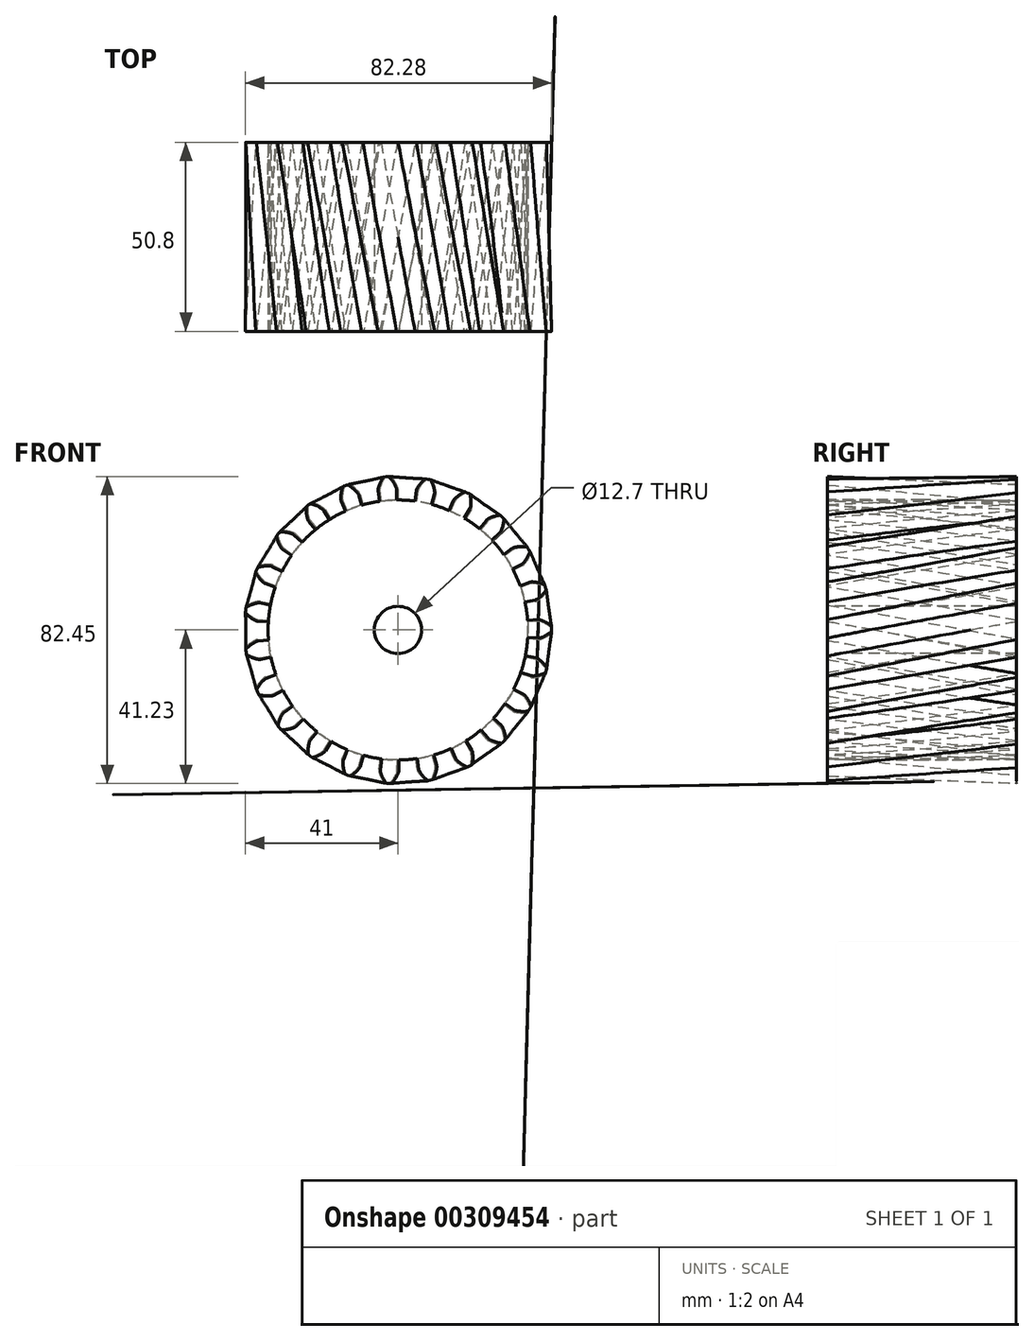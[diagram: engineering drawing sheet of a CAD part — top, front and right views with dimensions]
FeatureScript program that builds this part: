
annotation { "Feature Type Name" : "Feature", "Feature Type Description" : "" }
export const myFeature = defineFeature(function(context is Context, id is Id, definition is map)
    precondition{}
    {
        {
            var Q0;
            Q0=qCreatedBy(makeId("Front.planeOp"),FACE);
            var sketch = newSketch(context, id + "F0", { "sketchPlane" : qUnion([Q0])});
            skCircle(sketch, "E0", {"center": v(0, 0) * mm, "radius": 34.92 * mm});
            skArc(sketch, "E1", {"start": v(-0.13, 38.42) * mm, "mid": v(-0.86, 39.8) * mm, "end": v(-1.8, 41.05) * mm});
            skLineSegment(sketch, "E2", {"start": v(-2.2, 41.22) * mm, "end": v(-2.7, 41.2) * mm});
            skLineSegment(sketch, "E3", {"start": v(0, 37.79) * mm, "end": v(0, 34.92) * mm});
            skLineSegment(sketch, "E4.MirrorCS", {"start": v(-3.2, 41.15) * mm, "end": v(-2.7, 41.2) * mm});
            skArc(sketch, "E5.MirrorCS", {"start": v(-4.89, 38.1) * mm, "mid": v(-4.34, 39.57) * mm, "end": v(-3.57, 40.93) * mm});
            skLineSegment(sketch, "E6.MirrorCS", {"start": v(-4.93, 37.47) * mm, "end": v(-4.56, 34.63) * mm});
            skPoint(sketch, "E7.visualSharp", {"position": v(-4.97, 37.77) * mm});
            skArc(sketch, "E7.filletArc", {"start": v(-4.89, 38.1) * mm, "mid": v(-4.94, 37.79) * mm, "end": v(-4.93, 37.47) * mm});
            skPoint(sketch, "E8.visualSharp", {"position": v(0, 38.1) * mm});
            skArc(sketch, "E8.filletArc", {"start": v(0, 37.79) * mm, "mid": v(-0.03, 38.1) * mm, "end": v(-0.13, 38.42) * mm});
            skPoint(sketch, "E9.visualSharp", {"position": v(-3.43, 41.13) * mm});
            skArc(sketch, "E9.filletArc", {"start": v(-3.2, 41.15) * mm, "mid": v(-3.4, 41.09) * mm, "end": v(-3.57, 40.93) * mm});
            skPoint(sketch, "E10.visualSharp", {"position": v(-1.97, 41.23) * mm});
            skArc(sketch, "E10.filletArc", {"start": v(-1.8, 41.05) * mm, "mid": v(-1.99, 41.18) * mm, "end": v(-2.2, 41.22) * mm});
            skSolve(sketch);
        }
        {
            var Q0;
            Q0=qCreatedBy(makeId("Front.planeOp"),FACE);
            cPlane(context, id + "F1", {"entities" : qUnion([Q0]), "cplaneType" : CPlaneType.OFFSET, "offset" : 50.8 * mm, "width" : 152.4 * mm, "height" : 152.4 * mm});
        }
        {
            var Q0;
            Q0=qCreatedBy(id+"F1.planeOp",FACE);
            var sketch = newSketch(context, id + "F2", { "sketchPlane" : qUnion([Q0])});
            skCircle(sketch, "E11", {"center": v(0, 0) * mm, "radius": 34.92 * mm});
            skArc(sketch, "E12", {"start": v(-0.13, 38.42) * mm, "mid": v(-0.86, 39.8) * mm, "end": v(-1.8, 41.05) * mm});
            skLineSegment(sketch, "E13", {"start": v(-2.2, 41.22) * mm, "end": v(-2.7, 41.2) * mm});
            skLineSegment(sketch, "E14", {"start": v(0, 37.79) * mm, "end": v(0, 34.92) * mm});
            skLineSegment(sketch, "E15.MirrorCS", {"start": v(-3.2, 41.15) * mm, "end": v(-2.7, 41.2) * mm});
            skArc(sketch, "E16.MirrorCS", {"start": v(-4.89, 38.1) * mm, "mid": v(-4.34, 39.57) * mm, "end": v(-3.57, 40.93) * mm});
            skLineSegment(sketch, "E17.MirrorCS", {"start": v(-4.93, 37.47) * mm, "end": v(-4.56, 34.63) * mm});
            skPoint(sketch, "E18.visualSharp", {"position": v(-4.97, 37.77) * mm});
            skArc(sketch, "E18.filletArc", {"start": v(-4.89, 38.1) * mm, "mid": v(-4.94, 37.79) * mm, "end": v(-4.93, 37.47) * mm});
            skPoint(sketch, "E19.visualSharp", {"position": v(0, 38.1) * mm});
            skArc(sketch, "E19.filletArc", {"start": v(0, 37.79) * mm, "mid": v(-0.03, 38.1) * mm, "end": v(-0.13, 38.42) * mm});
            skPoint(sketch, "E20.visualSharp", {"position": v(-3.43, 41.13) * mm});
            skArc(sketch, "E20.filletArc", {"start": v(-3.2, 41.15) * mm, "mid": v(-3.4, 41.09) * mm, "end": v(-3.57, 40.93) * mm});
            skPoint(sketch, "E21.visualSharp", {"position": v(-1.97, 41.23) * mm});
            skArc(sketch, "E21.filletArc", {"start": v(-1.8, 41.05) * mm, "mid": v(-1.99, 41.18) * mm, "end": v(-2.2, 41.22) * mm});
            skLineSegment(sketch, "E22.1.0", {"start": v(-13.73, 38.92) * mm, "end": v(-13.27, 39.1) * mm});
            skLineSegment(sketch, "E22.1.1", {"start": v(-12.8, 39.24) * mm, "end": v(-13.27, 39.1) * mm});
            skArc(sketch, "E22.1.2", {"start": v(-12.37, 39.18) * mm, "mid": v(-12.58, 39.26) * mm, "end": v(-12.8, 39.24) * mm});
            skArc(sketch, "E22.1.3", {"start": v(-13.73, 38.92) * mm, "mid": v(-13.92, 38.8) * mm, "end": v(-14.04, 38.62) * mm});
            skArc(sketch, "E22.1.4", {"start": v(-14.58, 35.54) * mm, "mid": v(-14.44, 37.1) * mm, "end": v(-14.04, 38.62) * mm});
            skArc(sketch, "E22.1.5", {"start": v(-10.07, 37.07) * mm, "mid": v(-11.13, 38.22) * mm, "end": v(-12.37, 39.18) * mm});
            skArc(sketch, "E22.1.6", {"start": v(-9.78, 36.5) * mm, "mid": v(-9.9, 36.8) * mm, "end": v(-10.07, 37.07) * mm});
            skArc(sketch, "E22.1.7", {"start": v(-14.58, 35.54) * mm, "mid": v(-14.55, 35.22) * mm, "end": v(-14.46, 34.91) * mm});
            skLineSegment(sketch, "E22.1.8", {"start": v(-14.46, 34.91) * mm, "end": v(-13.37, 32.27) * mm});
            skLineSegment(sketch, "E22.1.9", {"start": v(-9.78, 36.5) * mm, "end": v(-9.04, 33.73) * mm});
            skLineSegment(sketch, "E22.2.0", {"start": v(-23.34, 34.04) * mm, "end": v(-22.93, 34.32) * mm});
            skLineSegment(sketch, "E22.2.1", {"start": v(-22.52, 34.6) * mm, "end": v(-22.93, 34.32) * mm});
            skArc(sketch, "E22.2.2", {"start": v(-22.09, 34.65) * mm, "mid": v(-22.31, 34.67) * mm, "end": v(-22.52, 34.6) * mm});
            skArc(sketch, "E22.2.3", {"start": v(-23.34, 34.04) * mm, "mid": v(-23.49, 33.88) * mm, "end": v(-23.56, 33.67) * mm});
            skArc(sketch, "E22.2.4", {"start": v(-23.28, 30.56) * mm, "mid": v(-23.55, 32.1) * mm, "end": v(-23.56, 33.67) * mm});
            skArc(sketch, "E22.2.5", {"start": v(-19.32, 33.2) * mm, "mid": v(-20.64, 34.04) * mm, "end": v(-22.09, 34.65) * mm});
            skArc(sketch, "E22.2.6", {"start": v(-18.9, 32.73) * mm, "mid": v(-19.08, 32.99) * mm, "end": v(-19.32, 33.2) * mm});
            skArc(sketch, "E22.2.7", {"start": v(-23.28, 30.56) * mm, "mid": v(-23.17, 30.25) * mm, "end": v(-23, 29.98) * mm});
            skLineSegment(sketch, "E22.2.8", {"start": v(-23, 29.98) * mm, "end": v(-21.26, 27.7) * mm});
            skLineSegment(sketch, "E22.2.9", {"start": v(-18.9, 32.73) * mm, "end": v(-17.46, 30.25) * mm});
            skLineSegment(sketch, "E22.3.0", {"start": v(-31.35, 26.84) * mm, "end": v(-31.04, 27.22) * mm});
            skLineSegment(sketch, "E22.3.1", {"start": v(-30.7, 27.58) * mm, "end": v(-31.04, 27.22) * mm});
            skArc(sketch, "E22.3.2", {"start": v(-30.3, 27.75) * mm, "mid": v(-30.52, 27.71) * mm, "end": v(-30.7, 27.58) * mm});
            skArc(sketch, "E22.3.3", {"start": v(-31.35, 26.84) * mm, "mid": v(-31.46, 26.65) * mm, "end": v(-31.47, 26.42) * mm});
            skArc(sketch, "E22.3.4", {"start": v(-30.4, 23.49) * mm, "mid": v(-31.05, 24.91) * mm, "end": v(-31.47, 26.42) * mm});
            skArc(sketch, "E22.3.5", {"start": v(-27.26, 27.07) * mm, "mid": v(-28.75, 27.54) * mm, "end": v(-30.3, 27.75) * mm});
            skArc(sketch, "E22.3.6", {"start": v(-26.72, 26.72) * mm, "mid": v(-26.97, 26.92) * mm, "end": v(-27.26, 27.07) * mm});
            skArc(sketch, "E22.3.7", {"start": v(-30.4, 23.49) * mm, "mid": v(-30.21, 23.22) * mm, "end": v(-29.98, 23) * mm});
            skLineSegment(sketch, "E22.3.8", {"start": v(-29.98, 23) * mm, "end": v(-27.7, 21.26) * mm});
            skLineSegment(sketch, "E22.3.9", {"start": v(-26.72, 26.72) * mm, "end": v(-24.7, 24.7) * mm});
            skLineSegment(sketch, "E22.4.0", {"start": v(-37.23, 17.81) * mm, "end": v(-37.02, 18.26) * mm});
            skLineSegment(sketch, "E22.4.1", {"start": v(-36.8, 18.7) * mm, "end": v(-37.02, 18.26) * mm});
            skArc(sketch, "E22.4.2", {"start": v(-36.45, 18.96) * mm, "mid": v(-36.66, 18.87) * mm, "end": v(-36.8, 18.7) * mm});
            skArc(sketch, "E22.4.3", {"start": v(-37.23, 17.81) * mm, "mid": v(-37.28, 17.6) * mm, "end": v(-37.23, 17.38) * mm});
            skArc(sketch, "E22.4.4", {"start": v(-35.44, 14.82) * mm, "mid": v(-36.44, 16.02) * mm, "end": v(-37.23, 17.38) * mm});
            skArc(sketch, "E22.4.5", {"start": v(-33.33, 19.1) * mm, "mid": v(-34.9, 19.16) * mm, "end": v(-36.45, 18.96) * mm});
            skArc(sketch, "E22.4.6", {"start": v(-32.73, 18.9) * mm, "mid": v(-33.02, 19.03) * mm, "end": v(-33.33, 19.1) * mm});
            skArc(sketch, "E22.4.7", {"start": v(-35.44, 14.82) * mm, "mid": v(-35.2, 14.61) * mm, "end": v(-34.91, 14.46) * mm});
            skLineSegment(sketch, "E22.4.8", {"start": v(-34.91, 14.46) * mm, "end": v(-32.27, 13.37) * mm});
            skLineSegment(sketch, "E22.4.9", {"start": v(-32.73, 18.9) * mm, "end": v(-30.25, 17.46) * mm});
            skLineSegment(sketch, "E22.5.0", {"start": v(-40.58, 7.57) * mm, "end": v(-40.49, 8.05) * mm});
            skLineSegment(sketch, "E22.5.1", {"start": v(-40.38, 8.53) * mm, "end": v(-40.49, 8.05) * mm});
            skArc(sketch, "E22.5.2", {"start": v(-40.12, 8.88) * mm, "mid": v(-40.29, 8.74) * mm, "end": v(-40.38, 8.53) * mm});
            skArc(sketch, "E22.5.3", {"start": v(-40.58, 7.57) * mm, "mid": v(-40.57, 7.35) * mm, "end": v(-40.46, 7.15) * mm});
            skArc(sketch, "E22.5.4", {"start": v(-38.07, 5.14) * mm, "mid": v(-39.35, 6.05) * mm, "end": v(-40.46, 7.15) * mm});
            skArc(sketch, "E22.5.5", {"start": v(-37.14, 9.82) * mm, "mid": v(-38.67, 9.47) * mm, "end": v(-40.12, 8.88) * mm});
            skArc(sketch, "E22.5.6", {"start": v(-36.5, 9.78) * mm, "mid": v(-36.82, 9.83) * mm, "end": v(-37.14, 9.82) * mm});
            skArc(sketch, "E22.5.7", {"start": v(-38.07, 5.14) * mm, "mid": v(-37.78, 5) * mm, "end": v(-37.47, 4.93) * mm});
            skLineSegment(sketch, "E22.5.8", {"start": v(-37.47, 4.93) * mm, "end": v(-34.63, 4.56) * mm});
            skLineSegment(sketch, "E22.5.9", {"start": v(-36.5, 9.78) * mm, "end": v(-33.73, 9.04) * mm});
            skLineSegment(sketch, "E22.6.0", {"start": v(-41.15, -3.2) * mm, "end": v(-41.2, -2.7) * mm});
            skLineSegment(sketch, "E22.6.1", {"start": v(-41.22, -2.2) * mm, "end": v(-41.2, -2.7) * mm});
            skArc(sketch, "E22.6.2", {"start": v(-41.05, -1.8) * mm, "mid": v(-41.18, -1.99) * mm, "end": v(-41.22, -2.2) * mm});
            skArc(sketch, "E22.6.3", {"start": v(-41.15, -3.2) * mm, "mid": v(-41.09, -3.4) * mm, "end": v(-40.93, -3.57) * mm});
            skArc(sketch, "E22.6.4", {"start": v(-38.1, -4.89) * mm, "mid": v(-39.57, -4.34) * mm, "end": v(-40.93, -3.57) * mm});
            skArc(sketch, "E22.6.5", {"start": v(-38.42, -0.13) * mm, "mid": v(-39.8, -0.86) * mm, "end": v(-41.05, -1.8) * mm});
            skArc(sketch, "E22.6.6", {"start": v(-37.79, 0) * mm, "mid": v(-38.1, -0.03) * mm, "end": v(-38.42, -0.13) * mm});
            skArc(sketch, "E22.6.7", {"start": v(-38.1, -4.89) * mm, "mid": v(-37.79, -4.94) * mm, "end": v(-37.47, -4.93) * mm});
            skLineSegment(sketch, "E22.6.8", {"start": v(-37.47, -4.93) * mm, "end": v(-34.63, -4.56) * mm});
            skLineSegment(sketch, "E22.6.9", {"start": v(-37.79, 0) * mm, "end": v(-34.92, 0) * mm});
            skLineSegment(sketch, "E22.7.0", {"start": v(-38.92, -13.73) * mm, "end": v(-39.1, -13.27) * mm});
            skLineSegment(sketch, "E22.7.1", {"start": v(-39.24, -12.8) * mm, "end": v(-39.1, -13.27) * mm});
            skArc(sketch, "E22.7.2", {"start": v(-39.18, -12.37) * mm, "mid": v(-39.26, -12.58) * mm, "end": v(-39.24, -12.8) * mm});
            skArc(sketch, "E22.7.3", {"start": v(-38.92, -13.73) * mm, "mid": v(-38.8, -13.92) * mm, "end": v(-38.62, -14.04) * mm});
            skArc(sketch, "E22.7.4", {"start": v(-35.54, -14.58) * mm, "mid": v(-37.1, -14.44) * mm, "end": v(-38.62, -14.04) * mm});
            skArc(sketch, "E22.7.5", {"start": v(-37.07, -10.07) * mm, "mid": v(-38.22, -11.13) * mm, "end": v(-39.18, -12.37) * mm});
            skArc(sketch, "E22.7.6", {"start": v(-36.5, -9.78) * mm, "mid": v(-36.8, -9.9) * mm, "end": v(-37.07, -10.07) * mm});
            skArc(sketch, "E22.7.7", {"start": v(-35.54, -14.58) * mm, "mid": v(-35.22, -14.55) * mm, "end": v(-34.91, -14.46) * mm});
            skLineSegment(sketch, "E22.7.8", {"start": v(-34.91, -14.46) * mm, "end": v(-32.27, -13.37) * mm});
            skLineSegment(sketch, "E22.7.9", {"start": v(-36.5, -9.78) * mm, "end": v(-33.73, -9.04) * mm});
            skLineSegment(sketch, "E22.8.0", {"start": v(-34.04, -23.34) * mm, "end": v(-34.32, -22.93) * mm});
            skLineSegment(sketch, "E22.8.1", {"start": v(-34.6, -22.52) * mm, "end": v(-34.32, -22.93) * mm});
            skArc(sketch, "E22.8.2", {"start": v(-34.65, -22.09) * mm, "mid": v(-34.67, -22.31) * mm, "end": v(-34.6, -22.52) * mm});
            skArc(sketch, "E22.8.3", {"start": v(-34.04, -23.34) * mm, "mid": v(-33.88, -23.49) * mm, "end": v(-33.67, -23.56) * mm});
            skArc(sketch, "E22.8.4", {"start": v(-30.56, -23.28) * mm, "mid": v(-32.1, -23.55) * mm, "end": v(-33.67, -23.56) * mm});
            skArc(sketch, "E22.8.5", {"start": v(-33.2, -19.32) * mm, "mid": v(-34.04, -20.64) * mm, "end": v(-34.65, -22.09) * mm});
            skArc(sketch, "E22.8.6", {"start": v(-32.73, -18.9) * mm, "mid": v(-32.99, -19.08) * mm, "end": v(-33.2, -19.32) * mm});
            skArc(sketch, "E22.8.7", {"start": v(-30.56, -23.28) * mm, "mid": v(-30.25, -23.17) * mm, "end": v(-29.98, -23) * mm});
            skLineSegment(sketch, "E22.8.8", {"start": v(-29.98, -23) * mm, "end": v(-27.7, -21.26) * mm});
            skLineSegment(sketch, "E22.8.9", {"start": v(-32.73, -18.9) * mm, "end": v(-30.25, -17.46) * mm});
            skLineSegment(sketch, "E22.9.0", {"start": v(-26.84, -31.35) * mm, "end": v(-27.22, -31.04) * mm});
            skLineSegment(sketch, "E22.9.1", {"start": v(-27.58, -30.7) * mm, "end": v(-27.22, -31.04) * mm});
            skArc(sketch, "E22.9.2", {"start": v(-27.75, -30.3) * mm, "mid": v(-27.71, -30.52) * mm, "end": v(-27.58, -30.7) * mm});
            skArc(sketch, "E22.9.3", {"start": v(-26.84, -31.35) * mm, "mid": v(-26.65, -31.46) * mm, "end": v(-26.42, -31.47) * mm});
            skArc(sketch, "E22.9.4", {"start": v(-23.49, -30.4) * mm, "mid": v(-24.91, -31.05) * mm, "end": v(-26.42, -31.47) * mm});
            skArc(sketch, "E22.9.5", {"start": v(-27.07, -27.26) * mm, "mid": v(-27.54, -28.75) * mm, "end": v(-27.75, -30.3) * mm});
            skArc(sketch, "E22.9.6", {"start": v(-26.72, -26.72) * mm, "mid": v(-26.92, -26.97) * mm, "end": v(-27.07, -27.26) * mm});
            skArc(sketch, "E22.9.7", {"start": v(-23.49, -30.4) * mm, "mid": v(-23.22, -30.21) * mm, "end": v(-23, -29.98) * mm});
            skLineSegment(sketch, "E22.9.8", {"start": v(-23, -29.98) * mm, "end": v(-21.26, -27.7) * mm});
            skLineSegment(sketch, "E22.9.9", {"start": v(-26.72, -26.72) * mm, "end": v(-24.7, -24.7) * mm});
            skLineSegment(sketch, "E22.10.0", {"start": v(-17.81, -37.23) * mm, "end": v(-18.26, -37.02) * mm});
            skLineSegment(sketch, "E22.10.1", {"start": v(-18.7, -36.8) * mm, "end": v(-18.26, -37.02) * mm});
            skArc(sketch, "E22.10.2", {"start": v(-18.96, -36.45) * mm, "mid": v(-18.87, -36.66) * mm, "end": v(-18.7, -36.8) * mm});
            skArc(sketch, "E22.10.3", {"start": v(-17.81, -37.23) * mm, "mid": v(-17.6, -37.28) * mm, "end": v(-17.38, -37.23) * mm});
            skArc(sketch, "E22.10.4", {"start": v(-14.82, -35.44) * mm, "mid": v(-16.02, -36.44) * mm, "end": v(-17.38, -37.23) * mm});
            skArc(sketch, "E22.10.5", {"start": v(-19.1, -33.33) * mm, "mid": v(-19.16, -34.9) * mm, "end": v(-18.96, -36.45) * mm});
            skArc(sketch, "E22.10.6", {"start": v(-18.9, -32.73) * mm, "mid": v(-19.03, -33.02) * mm, "end": v(-19.1, -33.33) * mm});
            skArc(sketch, "E22.10.7", {"start": v(-14.82, -35.44) * mm, "mid": v(-14.61, -35.2) * mm, "end": v(-14.46, -34.91) * mm});
            skLineSegment(sketch, "E22.10.8", {"start": v(-14.46, -34.91) * mm, "end": v(-13.37, -32.27) * mm});
            skLineSegment(sketch, "E22.10.9", {"start": v(-18.9, -32.73) * mm, "end": v(-17.46, -30.25) * mm});
            skLineSegment(sketch, "E22.11.0", {"start": v(-7.57, -40.58) * mm, "end": v(-8.05, -40.49) * mm});
            skLineSegment(sketch, "E22.11.1", {"start": v(-8.53, -40.38) * mm, "end": v(-8.05, -40.49) * mm});
            skArc(sketch, "E22.11.2", {"start": v(-8.88, -40.12) * mm, "mid": v(-8.74, -40.29) * mm, "end": v(-8.53, -40.38) * mm});
            skArc(sketch, "E22.11.3", {"start": v(-7.57, -40.58) * mm, "mid": v(-7.35, -40.57) * mm, "end": v(-7.15, -40.46) * mm});
            skArc(sketch, "E22.11.4", {"start": v(-5.14, -38.07) * mm, "mid": v(-6.05, -39.35) * mm, "end": v(-7.15, -40.46) * mm});
            skArc(sketch, "E22.11.5", {"start": v(-9.82, -37.14) * mm, "mid": v(-9.47, -38.67) * mm, "end": v(-8.88, -40.12) * mm});
            skArc(sketch, "E22.11.6", {"start": v(-9.78, -36.5) * mm, "mid": v(-9.83, -36.82) * mm, "end": v(-9.82, -37.14) * mm});
            skArc(sketch, "E22.11.7", {"start": v(-5.14, -38.07) * mm, "mid": v(-5, -37.78) * mm, "end": v(-4.93, -37.47) * mm});
            skLineSegment(sketch, "E22.11.8", {"start": v(-4.93, -37.47) * mm, "end": v(-4.56, -34.63) * mm});
            skLineSegment(sketch, "E22.11.9", {"start": v(-9.78, -36.5) * mm, "end": v(-9.04, -33.73) * mm});
            skLineSegment(sketch, "E22.12.0", {"start": v(3.2, -41.15) * mm, "end": v(2.7, -41.2) * mm});
            skLineSegment(sketch, "E22.12.1", {"start": v(2.2, -41.22) * mm, "end": v(2.7, -41.2) * mm});
            skArc(sketch, "E22.12.2", {"start": v(1.8, -41.05) * mm, "mid": v(1.99, -41.18) * mm, "end": v(2.2, -41.22) * mm});
            skArc(sketch, "E22.12.3", {"start": v(3.2, -41.15) * mm, "mid": v(3.4, -41.09) * mm, "end": v(3.57, -40.93) * mm});
            skArc(sketch, "E22.12.4", {"start": v(4.89, -38.1) * mm, "mid": v(4.34, -39.57) * mm, "end": v(3.57, -40.93) * mm});
            skArc(sketch, "E22.12.5", {"start": v(0.13, -38.42) * mm, "mid": v(0.86, -39.8) * mm, "end": v(1.8, -41.05) * mm});
            skArc(sketch, "E22.12.6", {"start": v(0, -37.79) * mm, "mid": v(0.03, -38.1) * mm, "end": v(0.13, -38.42) * mm});
            skArc(sketch, "E22.12.7", {"start": v(4.89, -38.1) * mm, "mid": v(4.94, -37.79) * mm, "end": v(4.93, -37.47) * mm});
            skLineSegment(sketch, "E22.12.8", {"start": v(4.93, -37.47) * mm, "end": v(4.56, -34.63) * mm});
            skLineSegment(sketch, "E22.12.9", {"start": v(0, -37.79) * mm, "end": v(0, -34.92) * mm});
            skLineSegment(sketch, "E22.13.0", {"start": v(13.73, -38.92) * mm, "end": v(13.27, -39.1) * mm});
            skLineSegment(sketch, "E22.13.1", {"start": v(12.8, -39.24) * mm, "end": v(13.27, -39.1) * mm});
            skArc(sketch, "E22.13.2", {"start": v(12.37, -39.18) * mm, "mid": v(12.58, -39.26) * mm, "end": v(12.8, -39.24) * mm});
            skArc(sketch, "E22.13.3", {"start": v(13.73, -38.92) * mm, "mid": v(13.92, -38.8) * mm, "end": v(14.04, -38.62) * mm});
            skArc(sketch, "E22.13.4", {"start": v(14.58, -35.54) * mm, "mid": v(14.44, -37.1) * mm, "end": v(14.04, -38.62) * mm});
            skArc(sketch, "E22.13.5", {"start": v(10.07, -37.07) * mm, "mid": v(11.13, -38.22) * mm, "end": v(12.37, -39.18) * mm});
            skArc(sketch, "E22.13.6", {"start": v(9.78, -36.5) * mm, "mid": v(9.9, -36.8) * mm, "end": v(10.07, -37.07) * mm});
            skArc(sketch, "E22.13.7", {"start": v(14.58, -35.54) * mm, "mid": v(14.55, -35.22) * mm, "end": v(14.46, -34.91) * mm});
            skLineSegment(sketch, "E22.13.8", {"start": v(14.46, -34.91) * mm, "end": v(13.37, -32.27) * mm});
            skLineSegment(sketch, "E22.13.9", {"start": v(9.78, -36.5) * mm, "end": v(9.04, -33.73) * mm});
            skLineSegment(sketch, "E22.14.0", {"start": v(23.34, -34.04) * mm, "end": v(22.93, -34.32) * mm});
            skLineSegment(sketch, "E22.14.1", {"start": v(22.52, -34.6) * mm, "end": v(22.93, -34.32) * mm});
            skArc(sketch, "E22.14.2", {"start": v(22.09, -34.65) * mm, "mid": v(22.31, -34.67) * mm, "end": v(22.52, -34.6) * mm});
            skArc(sketch, "E22.14.3", {"start": v(23.34, -34.04) * mm, "mid": v(23.49, -33.88) * mm, "end": v(23.56, -33.67) * mm});
            skArc(sketch, "E22.14.4", {"start": v(23.28, -30.56) * mm, "mid": v(23.55, -32.1) * mm, "end": v(23.56, -33.67) * mm});
            skArc(sketch, "E22.14.5", {"start": v(19.32, -33.2) * mm, "mid": v(20.64, -34.04) * mm, "end": v(22.09, -34.65) * mm});
            skArc(sketch, "E22.14.6", {"start": v(18.9, -32.73) * mm, "mid": v(19.08, -32.99) * mm, "end": v(19.32, -33.2) * mm});
            skArc(sketch, "E22.14.7", {"start": v(23.28, -30.56) * mm, "mid": v(23.17, -30.25) * mm, "end": v(23, -29.98) * mm});
            skLineSegment(sketch, "E22.14.8", {"start": v(23, -29.98) * mm, "end": v(21.26, -27.7) * mm});
            skLineSegment(sketch, "E22.14.9", {"start": v(18.9, -32.73) * mm, "end": v(17.46, -30.25) * mm});
            skLineSegment(sketch, "E22.15.0", {"start": v(31.35, -26.84) * mm, "end": v(31.04, -27.22) * mm});
            skLineSegment(sketch, "E22.15.1", {"start": v(30.7, -27.58) * mm, "end": v(31.04, -27.22) * mm});
            skArc(sketch, "E22.15.2", {"start": v(30.3, -27.75) * mm, "mid": v(30.52, -27.71) * mm, "end": v(30.7, -27.58) * mm});
            skArc(sketch, "E22.15.3", {"start": v(31.35, -26.84) * mm, "mid": v(31.46, -26.65) * mm, "end": v(31.47, -26.42) * mm});
            skArc(sketch, "E22.15.4", {"start": v(30.4, -23.49) * mm, "mid": v(31.05, -24.91) * mm, "end": v(31.47, -26.42) * mm});
            skArc(sketch, "E22.15.5", {"start": v(27.26, -27.07) * mm, "mid": v(28.75, -27.54) * mm, "end": v(30.3, -27.75) * mm});
            skArc(sketch, "E22.15.6", {"start": v(26.72, -26.72) * mm, "mid": v(26.97, -26.92) * mm, "end": v(27.26, -27.07) * mm});
            skArc(sketch, "E22.15.7", {"start": v(30.4, -23.49) * mm, "mid": v(30.21, -23.22) * mm, "end": v(29.98, -23) * mm});
            skLineSegment(sketch, "E22.15.8", {"start": v(29.98, -23) * mm, "end": v(27.7, -21.26) * mm});
            skLineSegment(sketch, "E22.15.9", {"start": v(26.72, -26.72) * mm, "end": v(24.7, -24.7) * mm});
            skLineSegment(sketch, "E22.16.0", {"start": v(37.23, -17.81) * mm, "end": v(37.02, -18.26) * mm});
            skLineSegment(sketch, "E22.16.1", {"start": v(36.8, -18.7) * mm, "end": v(37.02, -18.26) * mm});
            skArc(sketch, "E22.16.2", {"start": v(36.45, -18.96) * mm, "mid": v(36.66, -18.87) * mm, "end": v(36.8, -18.7) * mm});
            skArc(sketch, "E22.16.3", {"start": v(37.23, -17.81) * mm, "mid": v(37.28, -17.6) * mm, "end": v(37.23, -17.38) * mm});
            skArc(sketch, "E22.16.4", {"start": v(35.44, -14.82) * mm, "mid": v(36.44, -16.02) * mm, "end": v(37.23, -17.38) * mm});
            skArc(sketch, "E22.16.5", {"start": v(33.33, -19.1) * mm, "mid": v(34.9, -19.16) * mm, "end": v(36.45, -18.96) * mm});
            skArc(sketch, "E22.16.6", {"start": v(32.73, -18.9) * mm, "mid": v(33.02, -19.03) * mm, "end": v(33.33, -19.1) * mm});
            skArc(sketch, "E22.16.7", {"start": v(35.44, -14.82) * mm, "mid": v(35.2, -14.61) * mm, "end": v(34.91, -14.46) * mm});
            skLineSegment(sketch, "E22.16.8", {"start": v(34.91, -14.46) * mm, "end": v(32.27, -13.37) * mm});
            skLineSegment(sketch, "E22.16.9", {"start": v(32.73, -18.9) * mm, "end": v(30.25, -17.46) * mm});
            skLineSegment(sketch, "E22.17.0", {"start": v(40.58, -7.57) * mm, "end": v(40.49, -8.05) * mm});
            skLineSegment(sketch, "E22.17.1", {"start": v(40.38, -8.53) * mm, "end": v(40.49, -8.05) * mm});
            skArc(sketch, "E22.17.2", {"start": v(40.12, -8.88) * mm, "mid": v(40.29, -8.74) * mm, "end": v(40.38, -8.53) * mm});
            skArc(sketch, "E22.17.3", {"start": v(40.58, -7.57) * mm, "mid": v(40.57, -7.35) * mm, "end": v(40.46, -7.15) * mm});
            skArc(sketch, "E22.17.4", {"start": v(38.07, -5.14) * mm, "mid": v(39.35, -6.05) * mm, "end": v(40.46, -7.15) * mm});
            skArc(sketch, "E22.17.5", {"start": v(37.14, -9.82) * mm, "mid": v(38.67, -9.47) * mm, "end": v(40.12, -8.88) * mm});
            skArc(sketch, "E22.17.6", {"start": v(36.5, -9.78) * mm, "mid": v(36.82, -9.83) * mm, "end": v(37.14, -9.82) * mm});
            skArc(sketch, "E22.17.7", {"start": v(38.07, -5.14) * mm, "mid": v(37.78, -5) * mm, "end": v(37.47, -4.93) * mm});
            skLineSegment(sketch, "E22.17.8", {"start": v(37.47, -4.93) * mm, "end": v(34.63, -4.56) * mm});
            skLineSegment(sketch, "E22.17.9", {"start": v(36.5, -9.78) * mm, "end": v(33.73, -9.04) * mm});
            skLineSegment(sketch, "E22.18.0", {"start": v(41.15, 3.2) * mm, "end": v(41.2, 2.7) * mm});
            skLineSegment(sketch, "E22.18.1", {"start": v(41.22, 2.2) * mm, "end": v(41.2, 2.7) * mm});
            skArc(sketch, "E22.18.2", {"start": v(41.05, 1.8) * mm, "mid": v(41.18, 1.99) * mm, "end": v(41.22, 2.2) * mm});
            skArc(sketch, "E22.18.3", {"start": v(41.15, 3.2) * mm, "mid": v(41.09, 3.4) * mm, "end": v(40.93, 3.57) * mm});
            skArc(sketch, "E22.18.4", {"start": v(38.1, 4.89) * mm, "mid": v(39.57, 4.34) * mm, "end": v(40.93, 3.57) * mm});
            skArc(sketch, "E22.18.5", {"start": v(38.42, 0.13) * mm, "mid": v(39.8, 0.86) * mm, "end": v(41.05, 1.8) * mm});
            skArc(sketch, "E22.18.6", {"start": v(37.79, 0) * mm, "mid": v(38.1, 0.03) * mm, "end": v(38.42, 0.13) * mm});
            skArc(sketch, "E22.18.7", {"start": v(38.1, 4.89) * mm, "mid": v(37.79, 4.94) * mm, "end": v(37.47, 4.93) * mm});
            skLineSegment(sketch, "E22.18.8", {"start": v(37.47, 4.93) * mm, "end": v(34.63, 4.56) * mm});
            skLineSegment(sketch, "E22.18.9", {"start": v(37.79, 0) * mm, "end": v(34.92, 0) * mm});
            skLineSegment(sketch, "E22.19.0", {"start": v(38.92, 13.73) * mm, "end": v(39.1, 13.27) * mm});
            skLineSegment(sketch, "E22.19.1", {"start": v(39.24, 12.8) * mm, "end": v(39.1, 13.27) * mm});
            skArc(sketch, "E22.19.2", {"start": v(39.18, 12.37) * mm, "mid": v(39.26, 12.58) * mm, "end": v(39.24, 12.8) * mm});
            skArc(sketch, "E22.19.3", {"start": v(38.92, 13.73) * mm, "mid": v(38.8, 13.92) * mm, "end": v(38.62, 14.04) * mm});
            skArc(sketch, "E22.19.4", {"start": v(35.54, 14.58) * mm, "mid": v(37.1, 14.44) * mm, "end": v(38.62, 14.04) * mm});
            skArc(sketch, "E22.19.5", {"start": v(37.07, 10.07) * mm, "mid": v(38.22, 11.13) * mm, "end": v(39.18, 12.37) * mm});
            skArc(sketch, "E22.19.6", {"start": v(36.5, 9.78) * mm, "mid": v(36.8, 9.9) * mm, "end": v(37.07, 10.07) * mm});
            skArc(sketch, "E22.19.7", {"start": v(35.54, 14.58) * mm, "mid": v(35.22, 14.55) * mm, "end": v(34.91, 14.46) * mm});
            skLineSegment(sketch, "E22.19.8", {"start": v(34.91, 14.46) * mm, "end": v(32.27, 13.37) * mm});
            skLineSegment(sketch, "E22.19.9", {"start": v(36.5, 9.78) * mm, "end": v(33.73, 9.04) * mm});
            skLineSegment(sketch, "E22.20.0", {"start": v(34.04, 23.34) * mm, "end": v(34.32, 22.93) * mm});
            skLineSegment(sketch, "E22.20.1", {"start": v(34.6, 22.52) * mm, "end": v(34.32, 22.93) * mm});
            skArc(sketch, "E22.20.2", {"start": v(34.65, 22.09) * mm, "mid": v(34.67, 22.31) * mm, "end": v(34.6, 22.52) * mm});
            skArc(sketch, "E22.20.3", {"start": v(34.04, 23.34) * mm, "mid": v(33.88, 23.49) * mm, "end": v(33.67, 23.56) * mm});
            skArc(sketch, "E22.20.4", {"start": v(30.56, 23.28) * mm, "mid": v(32.1, 23.55) * mm, "end": v(33.67, 23.56) * mm});
            skArc(sketch, "E22.20.5", {"start": v(33.2, 19.32) * mm, "mid": v(34.04, 20.64) * mm, "end": v(34.65, 22.09) * mm});
            skArc(sketch, "E22.20.6", {"start": v(32.73, 18.9) * mm, "mid": v(32.99, 19.08) * mm, "end": v(33.2, 19.32) * mm});
            skArc(sketch, "E22.20.7", {"start": v(30.56, 23.28) * mm, "mid": v(30.25, 23.17) * mm, "end": v(29.98, 23) * mm});
            skLineSegment(sketch, "E22.20.8", {"start": v(29.98, 23) * mm, "end": v(27.7, 21.26) * mm});
            skLineSegment(sketch, "E22.20.9", {"start": v(32.73, 18.9) * mm, "end": v(30.25, 17.46) * mm});
            skLineSegment(sketch, "E22.21.0", {"start": v(26.84, 31.35) * mm, "end": v(27.22, 31.04) * mm});
            skLineSegment(sketch, "E22.21.1", {"start": v(27.58, 30.7) * mm, "end": v(27.22, 31.04) * mm});
            skArc(sketch, "E22.21.2", {"start": v(27.75, 30.3) * mm, "mid": v(27.71, 30.52) * mm, "end": v(27.58, 30.7) * mm});
            skArc(sketch, "E22.21.3", {"start": v(26.84, 31.35) * mm, "mid": v(26.65, 31.46) * mm, "end": v(26.42, 31.47) * mm});
            skArc(sketch, "E22.21.4", {"start": v(23.49, 30.4) * mm, "mid": v(24.91, 31.05) * mm, "end": v(26.42, 31.47) * mm});
            skArc(sketch, "E22.21.5", {"start": v(27.07, 27.26) * mm, "mid": v(27.54, 28.75) * mm, "end": v(27.75, 30.3) * mm});
            skArc(sketch, "E22.21.6", {"start": v(26.72, 26.72) * mm, "mid": v(26.92, 26.97) * mm, "end": v(27.07, 27.26) * mm});
            skArc(sketch, "E22.21.7", {"start": v(23.49, 30.4) * mm, "mid": v(23.22, 30.21) * mm, "end": v(23, 29.98) * mm});
            skLineSegment(sketch, "E22.21.8", {"start": v(23, 29.98) * mm, "end": v(21.26, 27.7) * mm});
            skLineSegment(sketch, "E22.21.9", {"start": v(26.72, 26.72) * mm, "end": v(24.7, 24.7) * mm});
            skLineSegment(sketch, "E22.22.0", {"start": v(17.81, 37.23) * mm, "end": v(18.26, 37.02) * mm});
            skLineSegment(sketch, "E22.22.1", {"start": v(18.7, 36.8) * mm, "end": v(18.26, 37.02) * mm});
            skArc(sketch, "E22.22.2", {"start": v(18.96, 36.45) * mm, "mid": v(18.87, 36.66) * mm, "end": v(18.7, 36.8) * mm});
            skArc(sketch, "E22.22.3", {"start": v(17.81, 37.23) * mm, "mid": v(17.6, 37.28) * mm, "end": v(17.38, 37.23) * mm});
            skArc(sketch, "E22.22.4", {"start": v(14.82, 35.44) * mm, "mid": v(16.02, 36.44) * mm, "end": v(17.38, 37.23) * mm});
            skArc(sketch, "E22.22.5", {"start": v(19.1, 33.33) * mm, "mid": v(19.16, 34.9) * mm, "end": v(18.96, 36.45) * mm});
            skArc(sketch, "E22.22.6", {"start": v(18.9, 32.73) * mm, "mid": v(19.03, 33.02) * mm, "end": v(19.1, 33.33) * mm});
            skArc(sketch, "E22.22.7", {"start": v(14.82, 35.44) * mm, "mid": v(14.61, 35.2) * mm, "end": v(14.46, 34.91) * mm});
            skLineSegment(sketch, "E22.22.8", {"start": v(14.46, 34.91) * mm, "end": v(13.37, 32.27) * mm});
            skLineSegment(sketch, "E22.22.9", {"start": v(18.9, 32.73) * mm, "end": v(17.46, 30.25) * mm});
            skLineSegment(sketch, "E22.23.0", {"start": v(7.57, 40.58) * mm, "end": v(8.05, 40.49) * mm});
            skLineSegment(sketch, "E22.23.1", {"start": v(8.53, 40.38) * mm, "end": v(8.05, 40.49) * mm});
            skArc(sketch, "E22.23.2", {"start": v(8.88, 40.12) * mm, "mid": v(8.74, 40.29) * mm, "end": v(8.53, 40.38) * mm});
            skArc(sketch, "E22.23.3", {"start": v(7.57, 40.58) * mm, "mid": v(7.35, 40.57) * mm, "end": v(7.15, 40.46) * mm});
            skArc(sketch, "E22.23.4", {"start": v(5.14, 38.07) * mm, "mid": v(6.05, 39.35) * mm, "end": v(7.15, 40.46) * mm});
            skArc(sketch, "E22.23.5", {"start": v(9.82, 37.14) * mm, "mid": v(9.47, 38.67) * mm, "end": v(8.88, 40.12) * mm});
            skArc(sketch, "E22.23.6", {"start": v(9.78, 36.5) * mm, "mid": v(9.83, 36.82) * mm, "end": v(9.82, 37.14) * mm});
            skArc(sketch, "E22.23.7", {"start": v(5.14, 38.07) * mm, "mid": v(5, 37.78) * mm, "end": v(4.93, 37.47) * mm});
            skLineSegment(sketch, "E22.23.8", {"start": v(4.93, 37.47) * mm, "end": v(4.56, 34.63) * mm});
            skLineSegment(sketch, "E22.23.9", {"start": v(9.78, 36.5) * mm, "end": v(9.04, 33.73) * mm});
            skSolve(sketch);
        }
        {
            var Q0;
            Q0=makeQuery(id+"F0.imprint","IMPRINT",FACE,{"disambiguationData":[TD([[makeQuery(id+"F0.imprint","IMPRINT",EDGE,{"derivedFrom":sQuery(id+"F0.wireOp",EDGE,"E1")}),1.0]])]});
            var Q1;
            Q1=makeQuery(id+"F2.imprint","IMPRINT",FACE,{"disambiguationData":[TD([[makeQuery(id+"F2.imprint","IMPRINT",EDGE,{"derivedFrom":sQuery(id+"F2.wireOp",EDGE,"E22.23.0")}),-1.0]])]});
            loft(context, id + "F3", {"sheetProfilesArray" : [{ "sheetProfileEntities" : qUnion([Q0]) }, { "sheetProfileEntities" : qUnion([Q1]) }]});
        }
        {
            var Q0;
            Q0=qCreatedBy(id+"F1.planeOp",FACE);
            var sketch = newSketch(context, id + "F4", { "sketchPlane" : qUnion([Q0])});
            skCircle(sketch, "E23", {"center": v(0, 0) * mm, "radius": 34.93 * mm});
            skSolve(sketch);
        }
        {
            var Q0;
            Q0=makeQuery(id+"F4.imprint","IMPRINT",FACE,{"disambiguationData":[TD([[makeQuery(id+"F4.imprint","IMPRINT",EDGE,{"derivedFrom":sQuery(id+"F4.wireOp",EDGE,"E23")}),1.0]])]});
            var Q1;
            Q1=makeQuery(id+"F3.opLoft","CAP_FACE",FACE,{"disambiguationData":[OSD([makeQuery(id+"F0.imprint","IMPRINT",FACE,{"disambiguationData":[TD([[makeQuery(id+"F0.imprint","IMPRINT",EDGE,{"derivedFrom":sQuery(id+"F0.wireOp",EDGE,"E1")}),1.0]])]})])],"isStart":true});
            extrude(context, id + "F5", {"entities" : qUnion([Q0]), "endBound" : BoundingType.UP_TO_SURFACE, "oppositeDirection" : true, "endBoundEntityFace" : qUnion([Q1]), "depth" : 25.4 * mm});
        }
        {
            var Q0;
            Q0=makeQuery(id+"F3.opLoft","SWEPT_BODY",BODY,{"disambiguationData":[OSD([makeQuery(id+"F0.imprint","IMPRINT",FACE,{"disambiguationData":[TD([[makeQuery(id+"F0.imprint","IMPRINT",EDGE,{"derivedFrom":sQuery(id+"F0.wireOp",EDGE,"E1")}),1.0]])]}),makeQuery(id+"F2.imprint","IMPRINT",FACE,{"disambiguationData":[TD([[makeQuery(id+"F2.imprint","IMPRINT",EDGE,{"derivedFrom":sQuery(id+"F2.wireOp",EDGE,"E22.23.0")}),-1.0]])]})])]});
            var Q1;
            Q1=makeQuery(id+"F5.opExtrude","CAP_EDGE",EDGE,{"disambiguationData":[OSD([sQuery(id+"F4.wireOp",EDGE,"E23")])],"isStart":false});
            circularPattern(context, id + "F6", {"entities" : qUnion([Q0]), "axis" : qUnion([Q1]), "angle" : 360 * degree, "instanceCount" : 23, "equalSpace" : true});
        }
        {
            var Q0;
            Q0=makeQuery(id+"F6.opPattern","COPY",BODY,{"derivedFrom":makeQuery(id+"F3.opLoft","SWEPT_BODY",BODY,{"disambiguationData":[OSD([makeQuery(id+"F0.imprint","IMPRINT",FACE,{"disambiguationData":[TD([[makeQuery(id+"F0.imprint","IMPRINT",EDGE,{"derivedFrom":sQuery(id+"F0.wireOp",EDGE,"E1")}),1.0]])]}),makeQuery(id+"F2.imprint","IMPRINT",FACE,{"disambiguationData":[TD([[makeQuery(id+"F2.imprint","IMPRINT",EDGE,{"derivedFrom":sQuery(id+"F2.wireOp",EDGE,"E22.23.0")}),-1.0]])]})])]}),"instanceName":"22"});
            var Q1;
            Q1=makeQuery(id+"F5.opExtrude","SWEPT_BODY",BODY,{"disambiguationData":[OSD([sQuery(id+"F4.wireOp",EDGE,"E23")])]});
            var Q2;
            Q2=makeQuery(id+"F3.opLoft","SWEPT_BODY",BODY,{"disambiguationData":[OSD([makeQuery(id+"F0.imprint","IMPRINT",FACE,{"disambiguationData":[TD([[makeQuery(id+"F0.imprint","IMPRINT",EDGE,{"derivedFrom":sQuery(id+"F0.wireOp",EDGE,"E1")}),1.0]])]}),makeQuery(id+"F2.imprint","IMPRINT",FACE,{"disambiguationData":[TD([[makeQuery(id+"F2.imprint","IMPRINT",EDGE,{"derivedFrom":sQuery(id+"F2.wireOp",EDGE,"E22.23.0")}),-1.0]])]})])]});
            var Q3;
            Q3=makeQuery(id+"F6.opPattern","COPY",BODY,{"derivedFrom":makeQuery(id+"F3.opLoft","SWEPT_BODY",BODY,{"disambiguationData":[OSD([makeQuery(id+"F0.imprint","IMPRINT",FACE,{"disambiguationData":[TD([[makeQuery(id+"F0.imprint","IMPRINT",EDGE,{"derivedFrom":sQuery(id+"F0.wireOp",EDGE,"E1")}),1.0]])]}),makeQuery(id+"F2.imprint","IMPRINT",FACE,{"disambiguationData":[TD([[makeQuery(id+"F2.imprint","IMPRINT",EDGE,{"derivedFrom":sQuery(id+"F2.wireOp",EDGE,"E22.23.0")}),-1.0]])]})])]}),"instanceName":"1"});
            var Q4;
            Q4=makeQuery(id+"F6.opPattern","COPY",BODY,{"derivedFrom":makeQuery(id+"F3.opLoft","SWEPT_BODY",BODY,{"disambiguationData":[OSD([makeQuery(id+"F0.imprint","IMPRINT",FACE,{"disambiguationData":[TD([[makeQuery(id+"F0.imprint","IMPRINT",EDGE,{"derivedFrom":sQuery(id+"F0.wireOp",EDGE,"E1")}),1.0]])]}),makeQuery(id+"F2.imprint","IMPRINT",FACE,{"disambiguationData":[TD([[makeQuery(id+"F2.imprint","IMPRINT",EDGE,{"derivedFrom":sQuery(id+"F2.wireOp",EDGE,"E22.23.0")}),-1.0]])]})])]}),"instanceName":"2"});
            var Q5;
            Q5=makeQuery(id+"F6.opPattern","COPY",BODY,{"derivedFrom":makeQuery(id+"F3.opLoft","SWEPT_BODY",BODY,{"disambiguationData":[OSD([makeQuery(id+"F0.imprint","IMPRINT",FACE,{"disambiguationData":[TD([[makeQuery(id+"F0.imprint","IMPRINT",EDGE,{"derivedFrom":sQuery(id+"F0.wireOp",EDGE,"E1")}),1.0]])]}),makeQuery(id+"F2.imprint","IMPRINT",FACE,{"disambiguationData":[TD([[makeQuery(id+"F2.imprint","IMPRINT",EDGE,{"derivedFrom":sQuery(id+"F2.wireOp",EDGE,"E22.23.0")}),-1.0]])]})])]}),"instanceName":"3"});
            var Q6;
            Q6=makeQuery(id+"F6.opPattern","COPY",BODY,{"derivedFrom":makeQuery(id+"F3.opLoft","SWEPT_BODY",BODY,{"disambiguationData":[OSD([makeQuery(id+"F0.imprint","IMPRINT",FACE,{"disambiguationData":[TD([[makeQuery(id+"F0.imprint","IMPRINT",EDGE,{"derivedFrom":sQuery(id+"F0.wireOp",EDGE,"E1")}),1.0]])]}),makeQuery(id+"F2.imprint","IMPRINT",FACE,{"disambiguationData":[TD([[makeQuery(id+"F2.imprint","IMPRINT",EDGE,{"derivedFrom":sQuery(id+"F2.wireOp",EDGE,"E22.23.0")}),-1.0]])]})])]}),"instanceName":"4"});
            var Q7;
            Q7=makeQuery(id+"F6.opPattern","COPY",BODY,{"derivedFrom":makeQuery(id+"F3.opLoft","SWEPT_BODY",BODY,{"disambiguationData":[OSD([makeQuery(id+"F0.imprint","IMPRINT",FACE,{"disambiguationData":[TD([[makeQuery(id+"F0.imprint","IMPRINT",EDGE,{"derivedFrom":sQuery(id+"F0.wireOp",EDGE,"E1")}),1.0]])]}),makeQuery(id+"F2.imprint","IMPRINT",FACE,{"disambiguationData":[TD([[makeQuery(id+"F2.imprint","IMPRINT",EDGE,{"derivedFrom":sQuery(id+"F2.wireOp",EDGE,"E22.23.0")}),-1.0]])]})])]}),"instanceName":"5"});
            var Q8;
            Q8=makeQuery(id+"F6.opPattern","COPY",BODY,{"derivedFrom":makeQuery(id+"F3.opLoft","SWEPT_BODY",BODY,{"disambiguationData":[OSD([makeQuery(id+"F0.imprint","IMPRINT",FACE,{"disambiguationData":[TD([[makeQuery(id+"F0.imprint","IMPRINT",EDGE,{"derivedFrom":sQuery(id+"F0.wireOp",EDGE,"E1")}),1.0]])]}),makeQuery(id+"F2.imprint","IMPRINT",FACE,{"disambiguationData":[TD([[makeQuery(id+"F2.imprint","IMPRINT",EDGE,{"derivedFrom":sQuery(id+"F2.wireOp",EDGE,"E22.23.0")}),-1.0]])]})])]}),"instanceName":"6"});
            var Q9;
            Q9=makeQuery(id+"F6.opPattern","COPY",BODY,{"derivedFrom":makeQuery(id+"F3.opLoft","SWEPT_BODY",BODY,{"disambiguationData":[OSD([makeQuery(id+"F0.imprint","IMPRINT",FACE,{"disambiguationData":[TD([[makeQuery(id+"F0.imprint","IMPRINT",EDGE,{"derivedFrom":sQuery(id+"F0.wireOp",EDGE,"E1")}),1.0]])]}),makeQuery(id+"F2.imprint","IMPRINT",FACE,{"disambiguationData":[TD([[makeQuery(id+"F2.imprint","IMPRINT",EDGE,{"derivedFrom":sQuery(id+"F2.wireOp",EDGE,"E22.23.0")}),-1.0]])]})])]}),"instanceName":"7"});
            var Q10;
            Q10=makeQuery(id+"F6.opPattern","COPY",BODY,{"derivedFrom":makeQuery(id+"F3.opLoft","SWEPT_BODY",BODY,{"disambiguationData":[OSD([makeQuery(id+"F0.imprint","IMPRINT",FACE,{"disambiguationData":[TD([[makeQuery(id+"F0.imprint","IMPRINT",EDGE,{"derivedFrom":sQuery(id+"F0.wireOp",EDGE,"E1")}),1.0]])]}),makeQuery(id+"F2.imprint","IMPRINT",FACE,{"disambiguationData":[TD([[makeQuery(id+"F2.imprint","IMPRINT",EDGE,{"derivedFrom":sQuery(id+"F2.wireOp",EDGE,"E22.23.0")}),-1.0]])]})])]}),"instanceName":"8"});
            var Q11;
            Q11=makeQuery(id+"F6.opPattern","COPY",BODY,{"derivedFrom":makeQuery(id+"F3.opLoft","SWEPT_BODY",BODY,{"disambiguationData":[OSD([makeQuery(id+"F0.imprint","IMPRINT",FACE,{"disambiguationData":[TD([[makeQuery(id+"F0.imprint","IMPRINT",EDGE,{"derivedFrom":sQuery(id+"F0.wireOp",EDGE,"E1")}),1.0]])]}),makeQuery(id+"F2.imprint","IMPRINT",FACE,{"disambiguationData":[TD([[makeQuery(id+"F2.imprint","IMPRINT",EDGE,{"derivedFrom":sQuery(id+"F2.wireOp",EDGE,"E22.23.0")}),-1.0]])]})])]}),"instanceName":"9"});
            var Q12;
            Q12=makeQuery(id+"F6.opPattern","COPY",BODY,{"derivedFrom":makeQuery(id+"F3.opLoft","SWEPT_BODY",BODY,{"disambiguationData":[OSD([makeQuery(id+"F0.imprint","IMPRINT",FACE,{"disambiguationData":[TD([[makeQuery(id+"F0.imprint","IMPRINT",EDGE,{"derivedFrom":sQuery(id+"F0.wireOp",EDGE,"E1")}),1.0]])]}),makeQuery(id+"F2.imprint","IMPRINT",FACE,{"disambiguationData":[TD([[makeQuery(id+"F2.imprint","IMPRINT",EDGE,{"derivedFrom":sQuery(id+"F2.wireOp",EDGE,"E22.23.0")}),-1.0]])]})])]}),"instanceName":"10"});
            var Q13;
            Q13=makeQuery(id+"F6.opPattern","COPY",BODY,{"derivedFrom":makeQuery(id+"F3.opLoft","SWEPT_BODY",BODY,{"disambiguationData":[OSD([makeQuery(id+"F0.imprint","IMPRINT",FACE,{"disambiguationData":[TD([[makeQuery(id+"F0.imprint","IMPRINT",EDGE,{"derivedFrom":sQuery(id+"F0.wireOp",EDGE,"E1")}),1.0]])]}),makeQuery(id+"F2.imprint","IMPRINT",FACE,{"disambiguationData":[TD([[makeQuery(id+"F2.imprint","IMPRINT",EDGE,{"derivedFrom":sQuery(id+"F2.wireOp",EDGE,"E22.23.0")}),-1.0]])]})])]}),"instanceName":"11"});
            var Q14;
            Q14=makeQuery(id+"F6.opPattern","COPY",BODY,{"derivedFrom":makeQuery(id+"F3.opLoft","SWEPT_BODY",BODY,{"disambiguationData":[OSD([makeQuery(id+"F0.imprint","IMPRINT",FACE,{"disambiguationData":[TD([[makeQuery(id+"F0.imprint","IMPRINT",EDGE,{"derivedFrom":sQuery(id+"F0.wireOp",EDGE,"E1")}),1.0]])]}),makeQuery(id+"F2.imprint","IMPRINT",FACE,{"disambiguationData":[TD([[makeQuery(id+"F2.imprint","IMPRINT",EDGE,{"derivedFrom":sQuery(id+"F2.wireOp",EDGE,"E22.23.0")}),-1.0]])]})])]}),"instanceName":"12"});
            var Q15;
            Q15=makeQuery(id+"F6.opPattern","COPY",BODY,{"derivedFrom":makeQuery(id+"F3.opLoft","SWEPT_BODY",BODY,{"disambiguationData":[OSD([makeQuery(id+"F0.imprint","IMPRINT",FACE,{"disambiguationData":[TD([[makeQuery(id+"F0.imprint","IMPRINT",EDGE,{"derivedFrom":sQuery(id+"F0.wireOp",EDGE,"E1")}),1.0]])]}),makeQuery(id+"F2.imprint","IMPRINT",FACE,{"disambiguationData":[TD([[makeQuery(id+"F2.imprint","IMPRINT",EDGE,{"derivedFrom":sQuery(id+"F2.wireOp",EDGE,"E22.23.0")}),-1.0]])]})])]}),"instanceName":"13"});
            var Q16;
            Q16=makeQuery(id+"F6.opPattern","COPY",BODY,{"derivedFrom":makeQuery(id+"F3.opLoft","SWEPT_BODY",BODY,{"disambiguationData":[OSD([makeQuery(id+"F0.imprint","IMPRINT",FACE,{"disambiguationData":[TD([[makeQuery(id+"F0.imprint","IMPRINT",EDGE,{"derivedFrom":sQuery(id+"F0.wireOp",EDGE,"E1")}),1.0]])]}),makeQuery(id+"F2.imprint","IMPRINT",FACE,{"disambiguationData":[TD([[makeQuery(id+"F2.imprint","IMPRINT",EDGE,{"derivedFrom":sQuery(id+"F2.wireOp",EDGE,"E22.23.0")}),-1.0]])]})])]}),"instanceName":"14"});
            var Q17;
            Q17=makeQuery(id+"F6.opPattern","COPY",BODY,{"derivedFrom":makeQuery(id+"F3.opLoft","SWEPT_BODY",BODY,{"disambiguationData":[OSD([makeQuery(id+"F0.imprint","IMPRINT",FACE,{"disambiguationData":[TD([[makeQuery(id+"F0.imprint","IMPRINT",EDGE,{"derivedFrom":sQuery(id+"F0.wireOp",EDGE,"E1")}),1.0]])]}),makeQuery(id+"F2.imprint","IMPRINT",FACE,{"disambiguationData":[TD([[makeQuery(id+"F2.imprint","IMPRINT",EDGE,{"derivedFrom":sQuery(id+"F2.wireOp",EDGE,"E22.23.0")}),-1.0]])]})])]}),"instanceName":"15"});
            var Q18;
            Q18=makeQuery(id+"F6.opPattern","COPY",BODY,{"derivedFrom":makeQuery(id+"F3.opLoft","SWEPT_BODY",BODY,{"disambiguationData":[OSD([makeQuery(id+"F0.imprint","IMPRINT",FACE,{"disambiguationData":[TD([[makeQuery(id+"F0.imprint","IMPRINT",EDGE,{"derivedFrom":sQuery(id+"F0.wireOp",EDGE,"E1")}),1.0]])]}),makeQuery(id+"F2.imprint","IMPRINT",FACE,{"disambiguationData":[TD([[makeQuery(id+"F2.imprint","IMPRINT",EDGE,{"derivedFrom":sQuery(id+"F2.wireOp",EDGE,"E22.23.0")}),-1.0]])]})])]}),"instanceName":"16"});
            var Q19;
            Q19=makeQuery(id+"F6.opPattern","COPY",BODY,{"derivedFrom":makeQuery(id+"F3.opLoft","SWEPT_BODY",BODY,{"disambiguationData":[OSD([makeQuery(id+"F0.imprint","IMPRINT",FACE,{"disambiguationData":[TD([[makeQuery(id+"F0.imprint","IMPRINT",EDGE,{"derivedFrom":sQuery(id+"F0.wireOp",EDGE,"E1")}),1.0]])]}),makeQuery(id+"F2.imprint","IMPRINT",FACE,{"disambiguationData":[TD([[makeQuery(id+"F2.imprint","IMPRINT",EDGE,{"derivedFrom":sQuery(id+"F2.wireOp",EDGE,"E22.23.0")}),-1.0]])]})])]}),"instanceName":"17"});
            var Q20;
            Q20=makeQuery(id+"F6.opPattern","COPY",BODY,{"derivedFrom":makeQuery(id+"F3.opLoft","SWEPT_BODY",BODY,{"disambiguationData":[OSD([makeQuery(id+"F0.imprint","IMPRINT",FACE,{"disambiguationData":[TD([[makeQuery(id+"F0.imprint","IMPRINT",EDGE,{"derivedFrom":sQuery(id+"F0.wireOp",EDGE,"E1")}),1.0]])]}),makeQuery(id+"F2.imprint","IMPRINT",FACE,{"disambiguationData":[TD([[makeQuery(id+"F2.imprint","IMPRINT",EDGE,{"derivedFrom":sQuery(id+"F2.wireOp",EDGE,"E22.23.0")}),-1.0]])]})])]}),"instanceName":"18"});
            var Q21;
            Q21=makeQuery(id+"F6.opPattern","COPY",BODY,{"derivedFrom":makeQuery(id+"F3.opLoft","SWEPT_BODY",BODY,{"disambiguationData":[OSD([makeQuery(id+"F0.imprint","IMPRINT",FACE,{"disambiguationData":[TD([[makeQuery(id+"F0.imprint","IMPRINT",EDGE,{"derivedFrom":sQuery(id+"F0.wireOp",EDGE,"E1")}),1.0]])]}),makeQuery(id+"F2.imprint","IMPRINT",FACE,{"disambiguationData":[TD([[makeQuery(id+"F2.imprint","IMPRINT",EDGE,{"derivedFrom":sQuery(id+"F2.wireOp",EDGE,"E22.23.0")}),-1.0]])]})])]}),"instanceName":"19"});
            var Q22;
            Q22=makeQuery(id+"F6.opPattern","COPY",BODY,{"derivedFrom":makeQuery(id+"F3.opLoft","SWEPT_BODY",BODY,{"disambiguationData":[OSD([makeQuery(id+"F0.imprint","IMPRINT",FACE,{"disambiguationData":[TD([[makeQuery(id+"F0.imprint","IMPRINT",EDGE,{"derivedFrom":sQuery(id+"F0.wireOp",EDGE,"E1")}),1.0]])]}),makeQuery(id+"F2.imprint","IMPRINT",FACE,{"disambiguationData":[TD([[makeQuery(id+"F2.imprint","IMPRINT",EDGE,{"derivedFrom":sQuery(id+"F2.wireOp",EDGE,"E22.23.0")}),-1.0]])]})])]}),"instanceName":"20"});
            var Q23;
            Q23=makeQuery(id+"F6.opPattern","COPY",BODY,{"derivedFrom":makeQuery(id+"F3.opLoft","SWEPT_BODY",BODY,{"disambiguationData":[OSD([makeQuery(id+"F0.imprint","IMPRINT",FACE,{"disambiguationData":[TD([[makeQuery(id+"F0.imprint","IMPRINT",EDGE,{"derivedFrom":sQuery(id+"F0.wireOp",EDGE,"E1")}),1.0]])]}),makeQuery(id+"F2.imprint","IMPRINT",FACE,{"disambiguationData":[TD([[makeQuery(id+"F2.imprint","IMPRINT",EDGE,{"derivedFrom":sQuery(id+"F2.wireOp",EDGE,"E22.23.0")}),-1.0]])]})])]}),"instanceName":"21"});
            booleanBodies(context, id + "F7", {"operationType" : BooleanOperationType.UNION, "tools" : qUnion([Q0, Q1, Q2, Q3, Q4, Q5, Q6, Q7, Q8, Q9, Q10, Q11, Q12, Q13, Q14, Q15, Q16, Q17, Q18, Q19, Q20, Q21, Q22, Q23])});
        }
        {
            var Q0;
            {var subQ3=makeQuery(id+"F3.opLoft","CAP_FACE",FACE,{"disambiguationData":[OSD([makeQuery(id+"F2.imprint","IMPRINT",FACE,{"disambiguationData":[TD([[makeQuery(id+"F2.imprint","IMPRINT",EDGE,{"derivedFrom":sQuery(id+"F2.wireOp",EDGE,"E22.23.0")}),-1.0]])]})])],"isStart":true});Q0=makeQuery(id+"F7.opBoolean","MERGE",FACE,{"derivedFrom":[subQ3,makeQuery(id+"F5.opExtrude","CAP_FACE",FACE,{"disambiguationData":[OSD([sQuery(id+"F4.wireOp",EDGE,"E23")])],"isStart":true}),makeQuery(id+"F6.opPattern","COPY",FACE,{"derivedFrom":subQ3,"instanceName":"1"}),makeQuery(id+"F6.opPattern","COPY",FACE,{"derivedFrom":subQ3,"instanceName":"2"}),makeQuery(id+"F6.opPattern","COPY",FACE,{"derivedFrom":subQ3,"instanceName":"3"}),makeQuery(id+"F6.opPattern","COPY",FACE,{"derivedFrom":subQ3,"instanceName":"4"}),makeQuery(id+"F6.opPattern","COPY",FACE,{"derivedFrom":subQ3,"instanceName":"5"}),makeQuery(id+"F6.opPattern","COPY",FACE,{"derivedFrom":subQ3,"instanceName":"6"}),makeQuery(id+"F6.opPattern","COPY",FACE,{"derivedFrom":subQ3,"instanceName":"7"}),makeQuery(id+"F6.opPattern","COPY",FACE,{"derivedFrom":subQ3,"instanceName":"8"}),makeQuery(id+"F6.opPattern","COPY",FACE,{"derivedFrom":subQ3,"instanceName":"9"}),makeQuery(id+"F6.opPattern","COPY",FACE,{"derivedFrom":subQ3,"instanceName":"10"}),makeQuery(id+"F6.opPattern","COPY",FACE,{"derivedFrom":subQ3,"instanceName":"11"}),makeQuery(id+"F6.opPattern","COPY",FACE,{"derivedFrom":subQ3,"instanceName":"12"}),makeQuery(id+"F6.opPattern","COPY",FACE,{"derivedFrom":subQ3,"instanceName":"13"}),makeQuery(id+"F6.opPattern","COPY",FACE,{"derivedFrom":subQ3,"instanceName":"14"}),makeQuery(id+"F6.opPattern","COPY",FACE,{"derivedFrom":subQ3,"instanceName":"15"}),makeQuery(id+"F6.opPattern","COPY",FACE,{"derivedFrom":subQ3,"instanceName":"16"}),makeQuery(id+"F6.opPattern","COPY",FACE,{"derivedFrom":subQ3,"instanceName":"17"}),makeQuery(id+"F6.opPattern","COPY",FACE,{"derivedFrom":subQ3,"instanceName":"18"}),makeQuery(id+"F6.opPattern","COPY",FACE,{"derivedFrom":subQ3,"instanceName":"19"}),makeQuery(id+"F6.opPattern","COPY",FACE,{"derivedFrom":subQ3,"instanceName":"20"}),makeQuery(id+"F6.opPattern","COPY",FACE,{"derivedFrom":subQ3,"instanceName":"21"}),makeQuery(id+"F6.opPattern","COPY",FACE,{"derivedFrom":subQ3,"instanceName":"22"})]});}
            var sketch = newSketch(context, id + "F8", { "sketchPlane" : qUnion([Q0])});
            skCircle(sketch, "E24", {"center": v(0, 0) * mm, "radius": 6.35 * mm});
            skSolve(sketch);
        }
        {
            var Q0;
            Q0=makeQuery(id+"F8.imprint","IMPRINT",FACE,{"disambiguationData":[TD([[makeQuery(id+"F8.imprint","IMPRINT",EDGE,{"derivedFrom":sQuery(id+"F8.wireOp",EDGE,"E24")}),1.0]])]});
            extrude(context, id + "F9", {"entities" : qUnion([Q0]), "operationType" : NewBodyOperationType.REMOVE, "endBound" : BoundingType.THROUGH_ALL, "oppositeDirection" : true, "depth" : 25.4 * mm});
        }
    });
